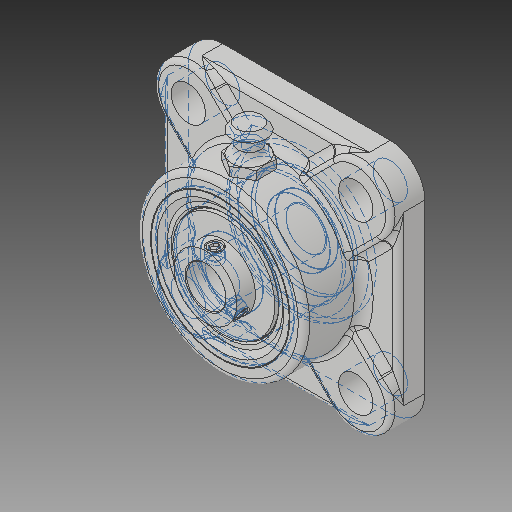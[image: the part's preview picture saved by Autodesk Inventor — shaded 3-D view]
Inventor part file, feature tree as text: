
AUTODESK INVENTOR PART (.ipt)
format: ipt  version: 2019 (Build 230136000, 136)  size: 728,064 bytes
history: native  units: in
note: dims shown in document units (in); Inventor stores cm internally (conversion verified against a paired STEP export)
features: other x2, pattern_circular x2, chamfer x1
ambient origin geometry x8: Origin, YZ Plane, XZ Plane, XY Plane, X Axis, Y Axis, Z Axis, Center Point
bodies: Solid1 (feature_tree), Solid2 (feature_tree), Solid3 (feature_tree), Solid4 (feature_tree), Solid5 (feature_tree)
feature tree (5):
  chamfer  "Chamfer3"  [1 undecoded]
  other  "Cut-Extrude3"
  pattern_circular  "CirPattern1"
  pattern_circular  "CirPattern2"
  other  "Cut-Extrude4"
note: 1 required parameter value undecoded (feature->parameter linkage not recoverable at this tier; creation-order binding heuristic only, values carry confidence <= 0.55)
